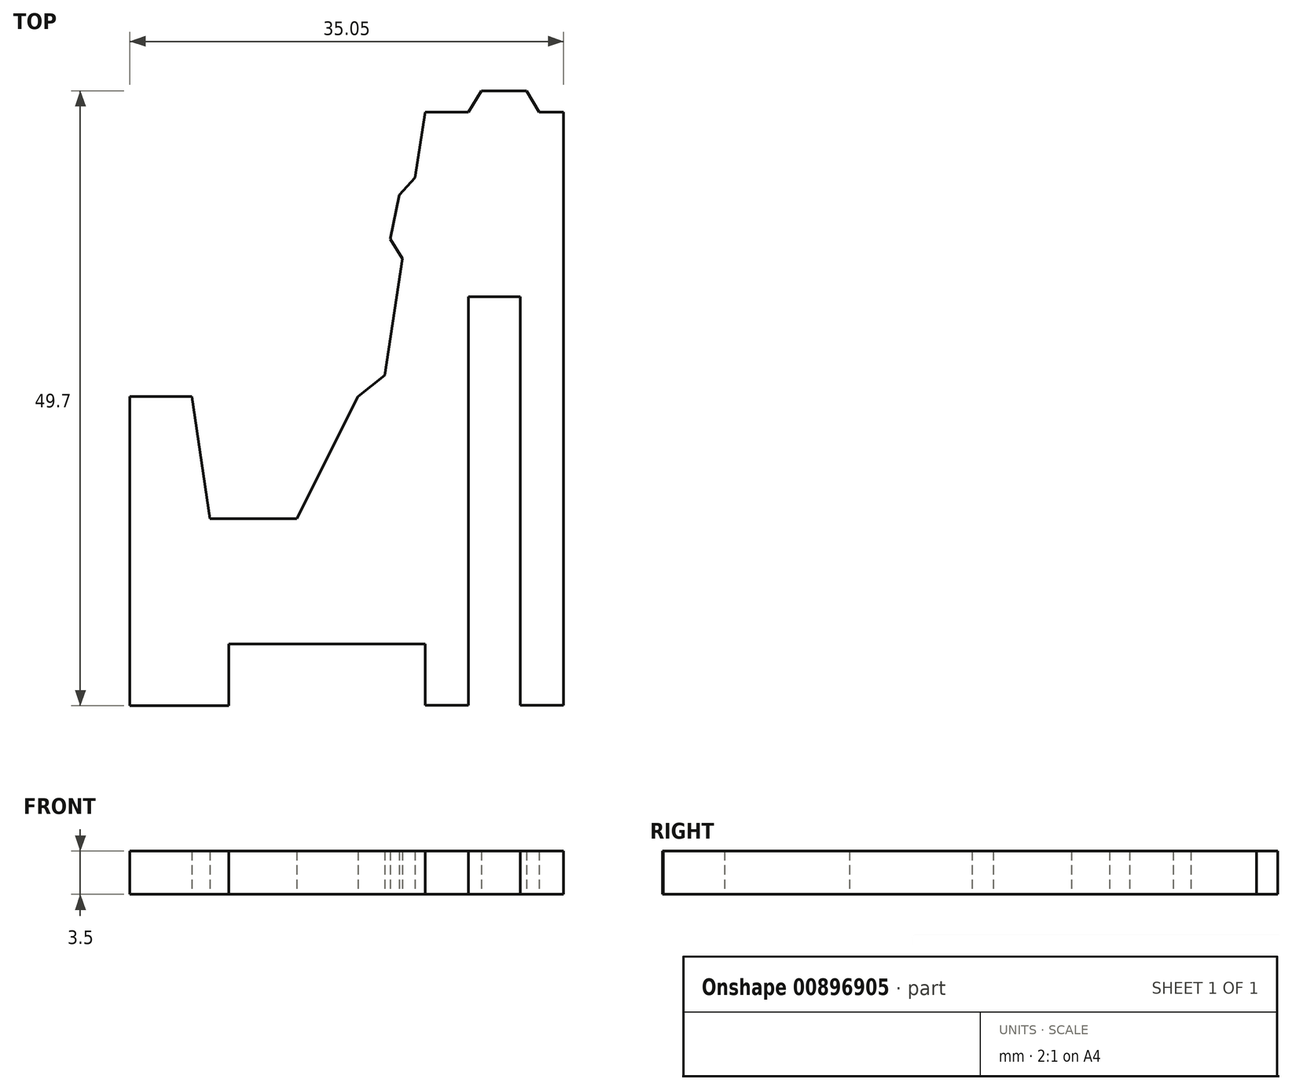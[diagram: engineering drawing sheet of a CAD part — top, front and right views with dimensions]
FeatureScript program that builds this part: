
annotation { "Feature Type Name" : "Feature", "Feature Type Description" : "" }
export const myFeature = defineFeature(function(context is Context, id is Id, definition is map)
    precondition{}
    {
        {
            var Q0;
            Q0=qCreatedBy(makeId("Top.planeOp"),FACE);
            var sketch = newSketch(context, id + "F0", { "sketchPlane" : qUnion([Q0])});
            skLineSegment(sketch, "E0", {"start": v(-12.35, -16.5) * mm, "end": v(-4.35, -16.5) * mm});
            skLineSegment(sketch, "E1", {"start": v(-4.35, -16.5) * mm, "end": v(-4.35, -11.5) * mm});
            skLineSegment(sketch, "E2", {"start": v(-12.35, -16.5) * mm, "end": v(-12.35, 8.5) * mm});
            skLineSegment(sketch, "E3", {"start": v(-12.35, 8.5) * mm, "end": v(-7.35, 8.5) * mm});
            skLineSegment(sketch, "E4", {"start": v(-7.35, 8.5) * mm, "end": v(-5.87, -1.4) * mm});
            skLineSegment(sketch, "E5", {"start": v(-5.87, -1.4) * mm, "end": v(1.13, -1.4) * mm});
            skLineSegment(sketch, "E6", {"start": v(1.13, -1.4) * mm, "end": v(6.1, 8.5) * mm});
            skLineSegment(sketch, "E7", {"start": v(6.1, 8.5) * mm, "end": v(8.24, 10.2) * mm});
            skLineSegment(sketch, "E8", {"start": v(8.24, 10.2) * mm, "end": v(9.68, 19.62) * mm});
            skLineSegment(sketch, "E9", {"start": v(22.7, -16.46) * mm, "end": v(22.7, 31.48) * mm});
            skLineSegment(sketch, "E10", {"start": v(11.5, 31.48) * mm, "end": v(15, 31.48) * mm});
            skLineSegment(sketch, "E11", {"start": v(22.7, 31.48) * mm, "end": v(20.73, 31.48) * mm});
            skPoint(sketch, "E12.start.orphan", {"position": v(9.87, 20.84) * mm});
            skLineSegment(sketch, "E13.trimOffspring", {"start": v(10.69, 26.18) * mm, "end": v(11.5, 31.48) * mm});
            skLineSegment(sketch, "E14", {"start": v(10.69, 26.18) * mm, "end": v(9.42, 24.76) * mm});
            skLineSegment(sketch, "E15", {"start": v(9.42, 24.76) * mm, "end": v(8.7, 21.22) * mm});
            skLineSegment(sketch, "E16", {"start": v(8.7, 21.22) * mm, "end": v(9.68, 19.62) * mm});
            skLineSegment(sketch, "E17", {"start": v(-4.35, -11.5) * mm, "end": v(11.5, -11.5) * mm});
            skLineSegment(sketch, "E18", {"start": v(11.5, -11.5) * mm, "end": v(11.5, -16.46) * mm});
            skLineSegment(sketch, "E19", {"start": v(11.5, -16.46) * mm, "end": v(15, -16.46) * mm});
            skLineSegment(sketch, "E20", {"start": v(22.7, -16.46) * mm, "end": v(19.2, -16.46) * mm});
            skLineSegment(sketch, "E21", {"start": v(15, -16.46) * mm, "end": v(15, 16.54) * mm});
            skLineSegment(sketch, "E22", {"start": v(19.2, -16.46) * mm, "end": v(19.2, 16.54) * mm});
            skLineSegment(sketch, "E23", {"start": v(15, 16.54) * mm, "end": v(19.2, 16.54) * mm});
            skLineSegment(sketch, "E24", {"start": v(15, 31.48) * mm, "end": v(16.04, 33.19) * mm});
            skLineSegment(sketch, "E25", {"start": v(20.73, 31.48) * mm, "end": v(19.69, 33.19) * mm});
            skLineSegment(sketch, "E26", {"start": v(19.69, 33.19) * mm, "end": v(16.04, 33.19) * mm});
            skSolve(sketch);
        }
        {
            var Q0;
            Q0 = qSketchRegion(id + "F0", true);
            extrude(context, id + "F1", {"entities" : qUnion([Q0]), "depth" : 3.5 * mm, "offsetDistance" : 25 * mm});
        }
    });
